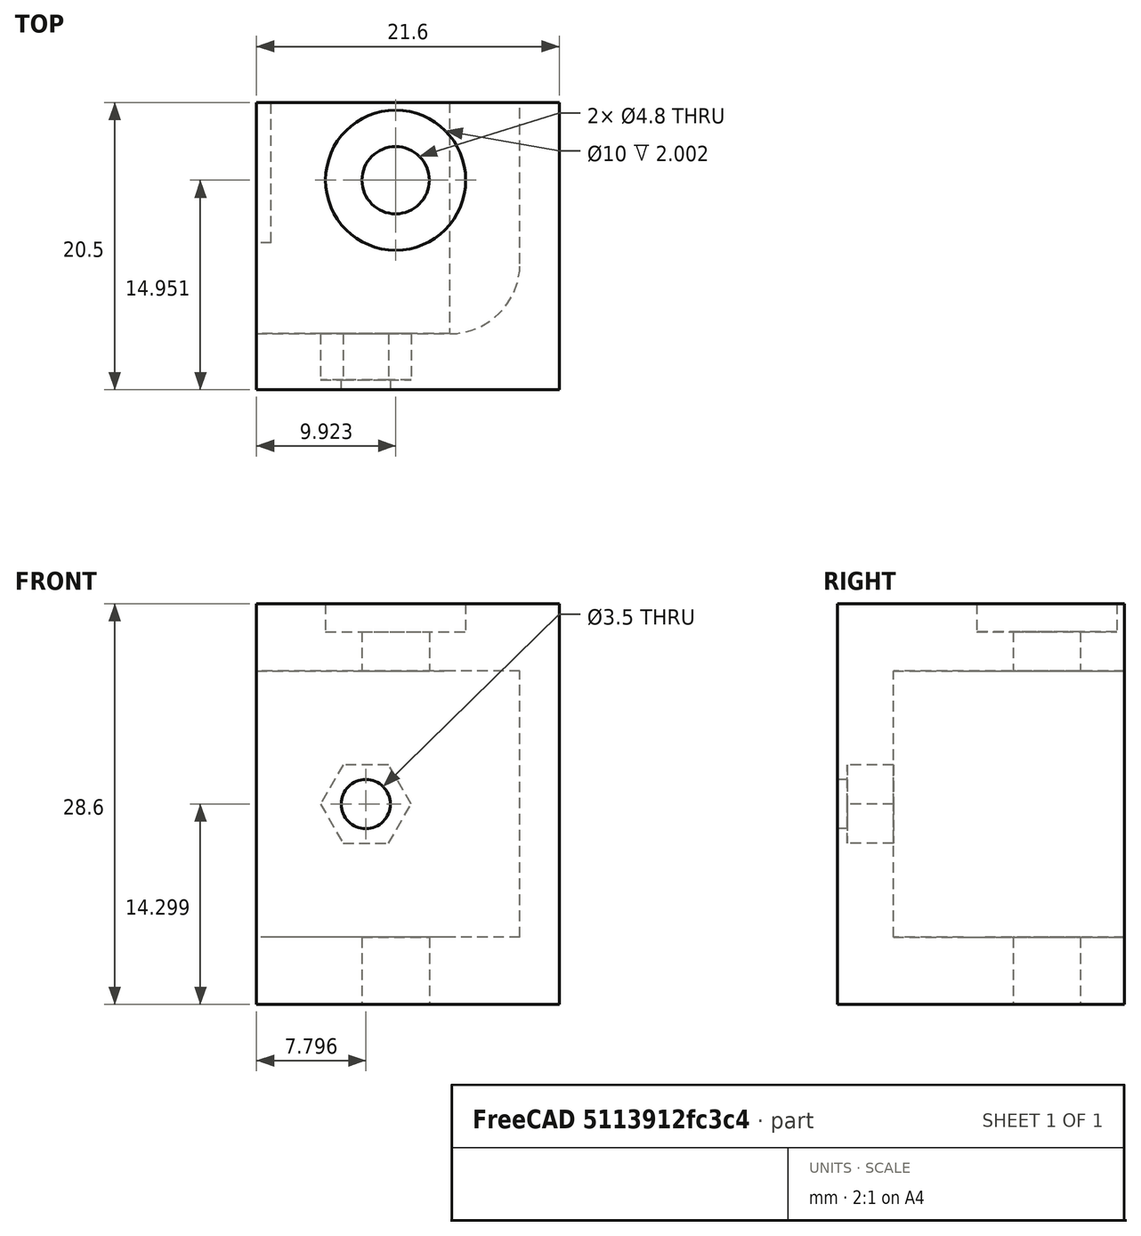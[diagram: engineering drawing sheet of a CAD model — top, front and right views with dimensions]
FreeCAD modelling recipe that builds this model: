
FCSTD DOCUMENT  (FreeCAD 2024.2R37179 (Git))
Label: Right_Idler_Cartridge
License: All rights reserved
LicenseURL: http://en.wikipedia.org/wiki/All_rights_reserved
objects: PartDesign::Pocket×2, Part::Feature×1, PartDesign::FeatureBase×1, PartDesign::Body×1
note: 7 computed .brp shape members not serialized (recipe doc carries the construction recipe); baked Part::Feature solids carry a one-line shape summary decoded from their .brp

FEATURE [Part::Feature] Part__Mirroring001  label="Pocket004 (Mirror #1)001"
  shape: bbox 23.6 x 20.5 x 28.6 mm, 34 faces (baked)
FEATURE [PartDesign::FeatureBase] BaseFeature
  BaseFeature = -> Part__Mirroring001
  Suppressed = false
FEATURE [PartDesign::Pocket] Pocket
  BaseFeature = -> BaseFeature
  Direction = (1,0,0)
  Length = 2
  Length2 = 5
  Profile = -> BaseFeature [Face5]
  Refine = true
  Suppressed = false
  Type = 0
FEATURE [PartDesign::Pocket] Pocket001
  BaseFeature = -> Pocket
  Direction = (-2e-16,1,-2e-16)
  Length = 14
  Length2 = 5
  Profile = -> Pocket [Face10]
  Refine = true
  Suppressed = false
  Type = 0
FEATURE [PartDesign::Body] Body
  BaseFeature = -> Part__Mirroring001
  Group = -> [BaseFeature,Pocket,Pocket001]
  Origin = -> Origin
  Tip = -> Pocket001
